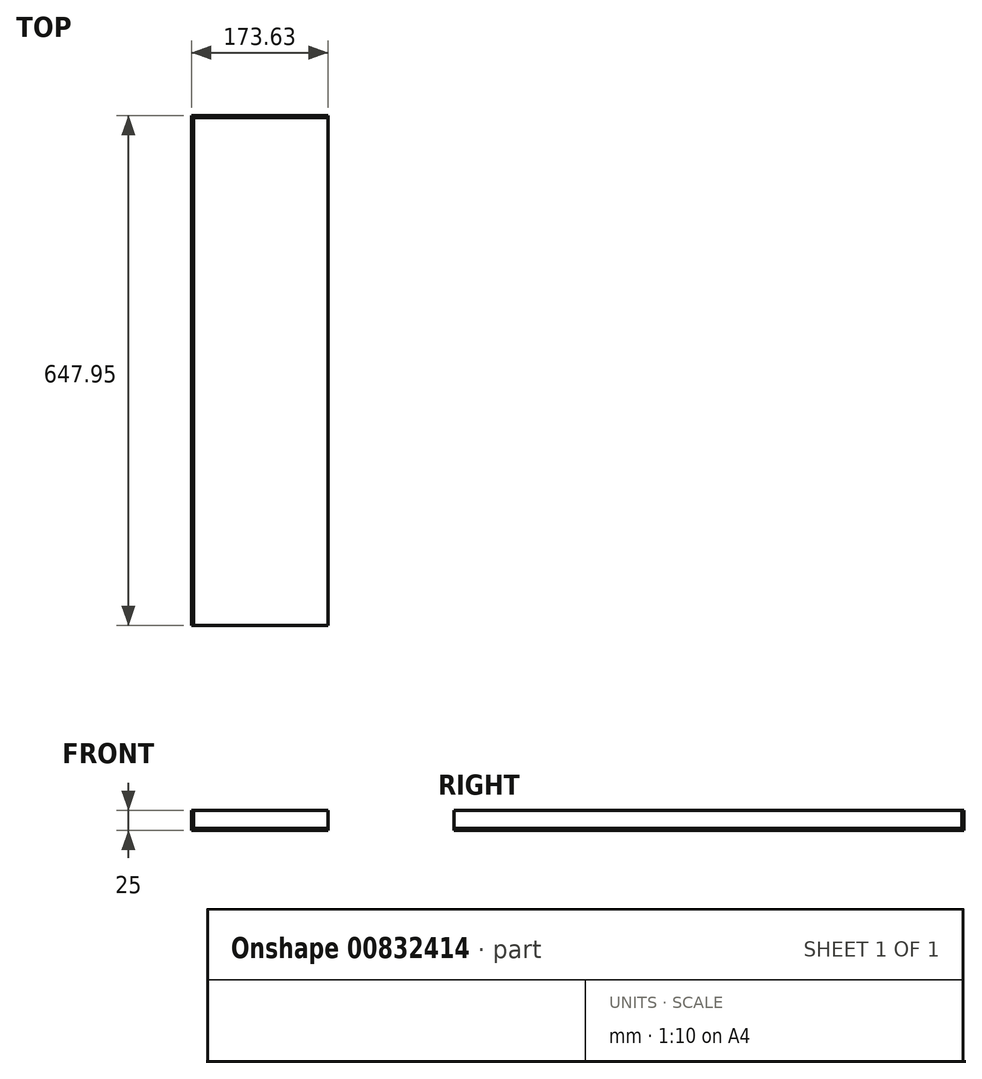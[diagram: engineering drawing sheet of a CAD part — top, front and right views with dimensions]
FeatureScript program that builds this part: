
annotation { "Feature Type Name" : "Feature", "Feature Type Description" : "" }
export const myFeature = defineFeature(function(context is Context, id is Id, definition is map)
    precondition{}
    {
        {
            var Q0;
            Q0=qCreatedBy(makeId("Top.planeOp"),FACE);
            var sketch = newSketch(context, id + "F0", { "sketchPlane" : qUnion([Q0])});
            skLineSegment(sketch, "E0.bottom", {"start": v(0, 0) * mm, "end": v(-173.63, 0) * mm});
            skLineSegment(sketch, "E0.top", {"start": v(0, 647.95) * mm, "end": v(-173.63, 647.95) * mm});
            skLineSegment(sketch, "E0.left", {"start": v(0, 0) * mm, "end": v(0, 647.95) * mm});
            skLineSegment(sketch, "E0.right", {"start": v(-173.63, 0) * mm, "end": v(-173.63, 647.95) * mm});
            skSolve(sketch);
        }
        {
            var Q0;
            Q0 = qSketchRegion(id + "F0", true);
            extrude(context, id + "F1", {"entities" : qUnion([Q0]), "depth" : 25 * mm, "offsetDistance" : 25 * mm});
        }
        {
            var Q0;
            Q0=makeQuery(id+"F1.opExtrude","SWEPT_FACE",FACE,{"disambiguationData":[OSD([sQuery(id+"F0.wireOp",EDGE,"E0.bottom")])]});
            var Q1;
            Q1=makeQuery(id+"F1.opExtrude","SWEPT_FACE",FACE,{"disambiguationData":[OSD([sQuery(id+"F0.wireOp",EDGE,"E0.left")])]});
            var Q2;
            Q2=makeQuery(id+"F1.opExtrude","CAP_FACE",FACE,{"disambiguationData":[OSD([sQuery(id+"F0.wireOp",EDGE,"E0.bottom"),sQuery(id+"F0.wireOp",EDGE,"E0.top"),sQuery(id+"F0.wireOp",EDGE,"E0.left"),sQuery(id+"F0.wireOp",EDGE,"E0.right")])],"isStart":false});
            shell(context, id + "F2", {"entities" : qUnion([Q0, Q1, Q2]), "thickness" : 2.5 * mm});
        }
    });
